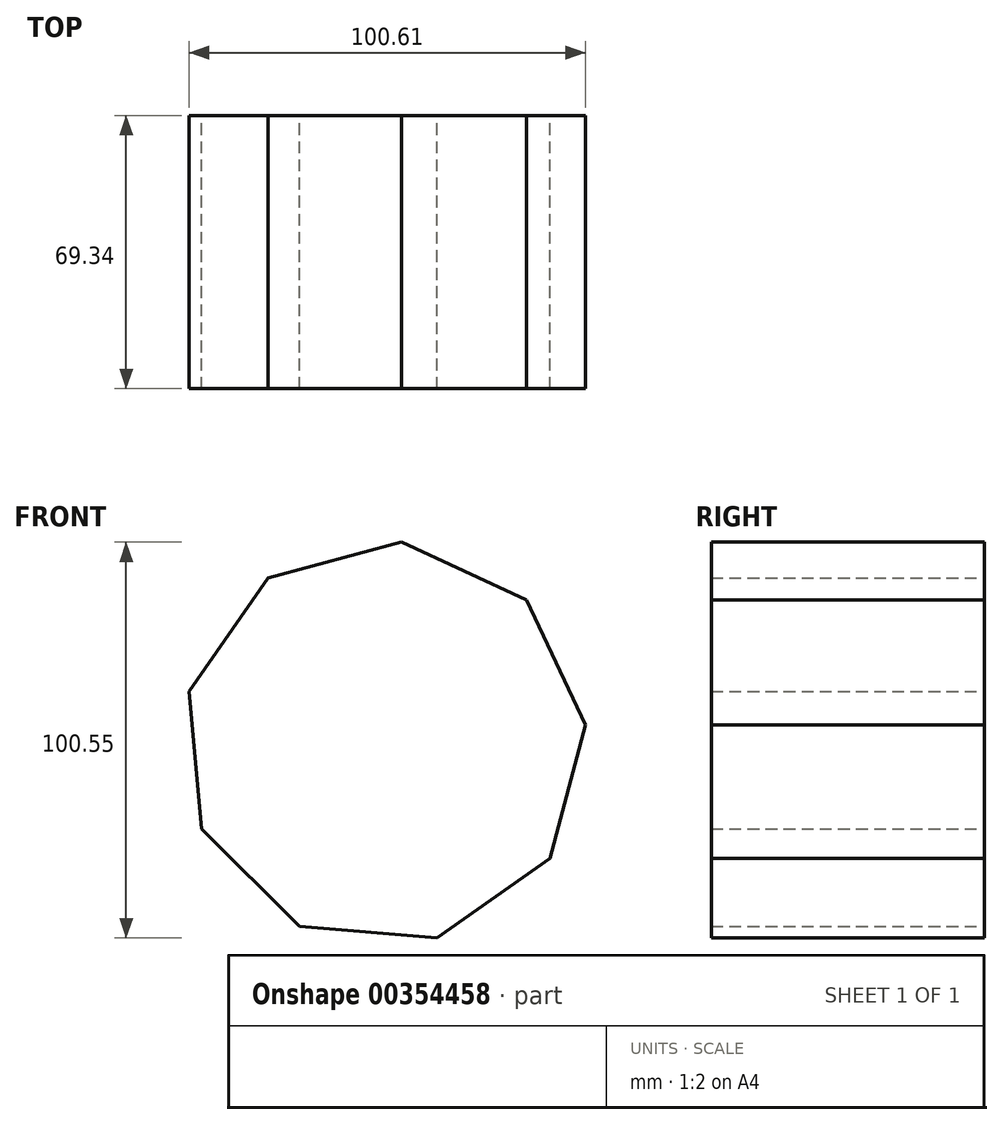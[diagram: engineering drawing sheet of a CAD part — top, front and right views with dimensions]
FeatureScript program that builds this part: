
annotation { "Feature Type Name" : "Feature", "Feature Type Description" : "" }
export const myFeature = defineFeature(function(context is Context, id is Id, definition is map)
    precondition{}
    {
        {
            var Q0;
            Q0=qCreatedBy(makeId("Front.planeOp"),FACE);
            var sketch = newSketch(context, id + "F0", { "sketchPlane" : qUnion([Q0])});
            skCircle(sketch, "E0.cCircle", {"center": v(0, 0) * mm, "radius": 51.26 * mm, "construction": true});
            skLineSegment(sketch, "E0.0", {"start": v(-46.4, -21.8) * mm, "end": v(-49.56, 13.12) * mm});
            skLineSegment(sketch, "E0.1", {"start": v(-49.56, 13.12) * mm, "end": v(-29.53, 41.9) * mm});
            skLineSegment(sketch, "E0.2", {"start": v(-29.53, 41.9) * mm, "end": v(4.31, 51.08) * mm});
            skLineSegment(sketch, "E0.3", {"start": v(4.31, 51.08) * mm, "end": v(36.14, 36.36) * mm});
            skLineSegment(sketch, "E0.4", {"start": v(36.14, 36.36) * mm, "end": v(51.05, 4.62) * mm});
            skLineSegment(sketch, "E0.5", {"start": v(51.05, 4.62) * mm, "end": v(42.08, -29.27) * mm});
            skLineSegment(sketch, "E0.6", {"start": v(42.08, -29.27) * mm, "end": v(13.42, -49.47) * mm});
            skLineSegment(sketch, "E0.7", {"start": v(13.42, -49.47) * mm, "end": v(-21.52, -46.52) * mm});
            skLineSegment(sketch, "E0.8", {"start": v(-21.52, -46.52) * mm, "end": v(-46.4, -21.8) * mm});
            skSolve(sketch);
        }
        {
            var Q0;
            Q0=makeQuery(id+"F0.imprint","IMPRINT",FACE,{"disambiguationData":[TD([[makeQuery(id+"F0.imprint","IMPRINT",EDGE,{"derivedFrom":sQuery(id+"F0.wireOp",EDGE,"E0.0")}),-1.0]])]});
            extrude(context, id + "F1", {"entities" : qUnion([Q0]), "depth" : 52.32 * mm});
        }
        {
            var Q0;
            Q0=makeQuery(id+"F1.opExtrude","CAP_FACE",FACE,{"disambiguationData":[OSD([sQuery(id+"F0.wireOp",EDGE,"E0.0"),sQuery(id+"F0.wireOp",EDGE,"E0.1"),sQuery(id+"F0.wireOp",EDGE,"E0.2"),sQuery(id+"F0.wireOp",EDGE,"E0.3"),sQuery(id+"F0.wireOp",EDGE,"E0.4"),sQuery(id+"F0.wireOp",EDGE,"E0.5"),sQuery(id+"F0.wireOp",EDGE,"E0.6"),sQuery(id+"F0.wireOp",EDGE,"E0.7"),sQuery(id+"F0.wireOp",EDGE,"E0.8")])],"isStart":false});
            var Q1;
            Q1=makeQuery(id+"F1.opExtrude","CAP_FACE",FACE,{"disambiguationData":[OSD([sQuery(id+"F0.wireOp",EDGE,"E0.0"),sQuery(id+"F0.wireOp",EDGE,"E0.1"),sQuery(id+"F0.wireOp",EDGE,"E0.2"),sQuery(id+"F0.wireOp",EDGE,"E0.3"),sQuery(id+"F0.wireOp",EDGE,"E0.4"),sQuery(id+"F0.wireOp",EDGE,"E0.5"),sQuery(id+"F0.wireOp",EDGE,"E0.6"),sQuery(id+"F0.wireOp",EDGE,"E0.7"),sQuery(id+"F0.wireOp",EDGE,"E0.8")])],"isStart":true});
            extrude(context, id + "F2", {"entities" : qUnion([Q0, Q1]), "operationType" : NewBodyOperationType.ADD, "oppositeDirection" : true, "depth" : 17.02 * mm});
        }
    });
